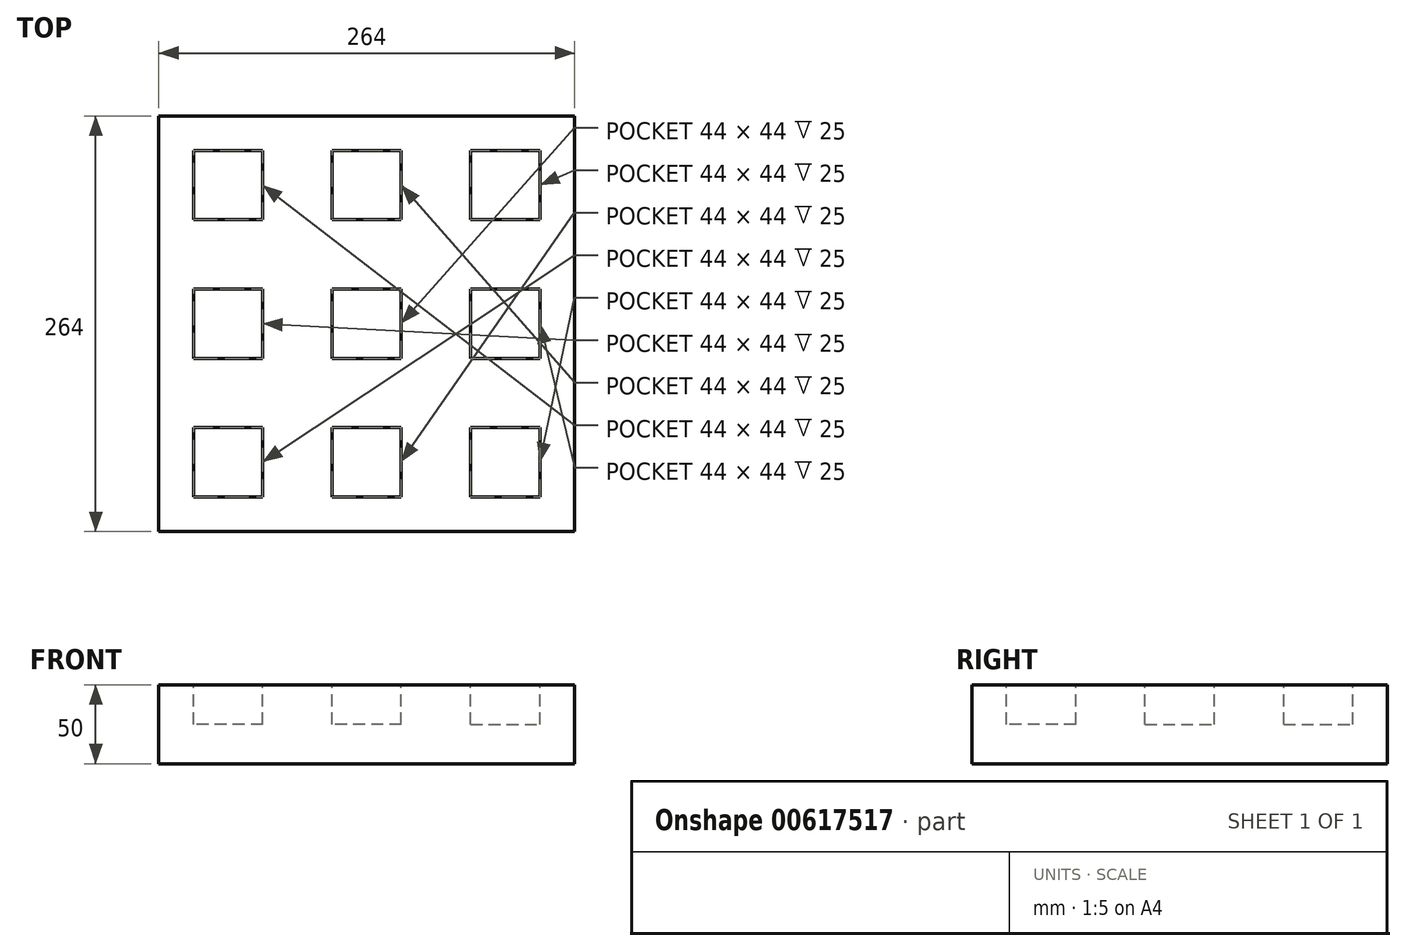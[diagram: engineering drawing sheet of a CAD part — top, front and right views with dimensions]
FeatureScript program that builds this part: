
annotation { "Feature Type Name" : "Feature", "Feature Type Description" : "" }
export const myFeature = defineFeature(function(context is Context, id is Id, definition is map)
    precondition{}
    {
        {
            var Q0;
            Q0=qCreatedBy(makeId("Top.planeOp"),FACE);
            var sketch = newSketch(context, id + "F0", { "sketchPlane" : qUnion([Q0])});
            skLineSegment(sketch, "E0.bottom", {"start": v(22, -22) * mm, "end": v(-22, -22) * mm});
            skLineSegment(sketch, "E0.top", {"start": v(22, 22) * mm, "end": v(-22, 22) * mm});
            skLineSegment(sketch, "E0.left", {"start": v(22, -22) * mm, "end": v(22, 22) * mm});
            skLineSegment(sketch, "E0.right", {"start": v(-22, -22) * mm, "end": v(-22, 22) * mm});
            skPoint(sketch, "E0.middle", {"position": v(0, 0) * mm});
            skLineSegment(sketch, "E1.bottom", {"start": v(-66, -22) * mm, "end": v(-110, -22) * mm});
            skLineSegment(sketch, "E1.top", {"start": v(-66, 22) * mm, "end": v(-110, 22) * mm});
            skLineSegment(sketch, "E1.left", {"start": v(-66, -22) * mm, "end": v(-66, 22) * mm});
            skLineSegment(sketch, "E1.right", {"start": v(-110, -22) * mm, "end": v(-110, 22) * mm});
            skPoint(sketch, "E1.middle", {"position": v(-88, 0) * mm});
            skPoint(sketch, "E1.middle.positionSnap0", {"position": v(-22, 0) * mm});
            skPoint(sketch, "E1.centerSnap0", {"position": v(-22, 0) * mm});
            skLineSegment(sketch, "E2.bottom", {"start": v(22, 66) * mm, "end": v(-22, 66) * mm});
            skLineSegment(sketch, "E2.top", {"start": v(22, 110) * mm, "end": v(-22, 110) * mm});
            skLineSegment(sketch, "E2.left", {"start": v(22, 66) * mm, "end": v(22, 110) * mm});
            skLineSegment(sketch, "E2.right", {"start": v(-22, 66) * mm, "end": v(-22, 110) * mm});
            skLineSegment(sketch, "E3.bottom", {"start": v(-66, 66) * mm, "end": v(-110, 66) * mm});
            skLineSegment(sketch, "E3.top", {"start": v(-66, 110) * mm, "end": v(-110, 110) * mm});
            skLineSegment(sketch, "E3.left", {"start": v(-66, 66) * mm, "end": v(-66, 110) * mm});
            skLineSegment(sketch, "E3.right", {"start": v(-110, 66) * mm, "end": v(-110, 110) * mm});
            skLineSegment(sketch, "E4.bottom", {"start": v(-132, 132) * mm, "end": v(132, 132) * mm});
            skLineSegment(sketch, "E4.top", {"start": v(-132, -132) * mm, "end": v(132, -132) * mm});
            skLineSegment(sketch, "E4.left", {"start": v(-132, 132) * mm, "end": v(-132, -132) * mm});
            skLineSegment(sketch, "E4.right", {"start": v(132, 132) * mm, "end": v(132, -132) * mm});
            skSolve(sketch);
        }
        {
            var Q0;
            Q0=makeQuery(id+"F0.imprint","IMPRINT",FACE,{"disambiguationData":[TD([[makeQuery(id+"F0.imprint","IMPRINT",EDGE,{"derivedFrom":sQuery(id+"F0.wireOp",EDGE,"E1.bottom")}),-1.0]])]});
            var Q1;
            Q1=makeQuery(id+"F0.imprint","IMPRINT",FACE,{"disambiguationData":[TD([[makeQuery(id+"F0.imprint","IMPRINT",EDGE,{"derivedFrom":sQuery(id+"F0.wireOp",EDGE,"E3.bottom")}),-1.0]])]});
            var Q2;
            Q2=makeQuery(id+"F0.imprint","IMPRINT",FACE,{"disambiguationData":[TD([[makeQuery(id+"F0.imprint","IMPRINT",EDGE,{"derivedFrom":sQuery(id+"F0.wireOp",EDGE,"E2.bottom")}),-1.0]])]});
            var Q3;
            Q3=makeQuery(id+"F0.imprint","IMPRINT",FACE,{"disambiguationData":[TD([[makeQuery(id+"F0.imprint","IMPRINT",EDGE,{"derivedFrom":sQuery(id+"F0.wireOp",EDGE,"E0.bottom")}),-1.0]])]});
            extrude(context, id + "F1", {"entities" : qUnion([Q0, Q1, Q2, Q3]), "oppositeDirection" : true, "depth" : 25 * mm, "offsetDistance" : 25 * mm});
        }
        {
            var Q0;
            Q0=makeQuery(id+"F1.opExtrude","SWEPT_BODY",BODY,{"disambiguationData":[OSD([sQuery(id+"F0.wireOp",EDGE,"E1.bottom"),sQuery(id+"F0.wireOp",EDGE,"E1.top"),sQuery(id+"F0.wireOp",EDGE,"E1.left"),sQuery(id+"F0.wireOp",EDGE,"E1.right")])]});
            var Q1;
            Q1=makeQuery(id+"F1.opExtrude","SWEPT_BODY",BODY,{"disambiguationData":[OSD([sQuery(id+"F0.wireOp",EDGE,"E3.bottom"),sQuery(id+"F0.wireOp",EDGE,"E3.top"),sQuery(id+"F0.wireOp",EDGE,"E3.left"),sQuery(id+"F0.wireOp",EDGE,"E3.right")])]});
            var Q2;
            Q2=qCreatedBy(makeId("Right.planeOp"),FACE);
            mirror(context, id + "F2", {"entities" : qUnion([Q0, Q1]), "mirrorPlane" : qUnion([Q2])});
        }
        {
            var Q0;
            Q0=makeQuery(id+"F1.opExtrude","SWEPT_BODY",BODY,{"disambiguationData":[OSD([sQuery(id+"F0.wireOp",EDGE,"E3.bottom"),sQuery(id+"F0.wireOp",EDGE,"E3.top"),sQuery(id+"F0.wireOp",EDGE,"E3.left"),sQuery(id+"F0.wireOp",EDGE,"E3.right")])]});
            var Q1;
            Q1=makeQuery(id+"F1.opExtrude","SWEPT_BODY",BODY,{"disambiguationData":[OSD([sQuery(id+"F0.wireOp",EDGE,"E2.bottom"),sQuery(id+"F0.wireOp",EDGE,"E2.top"),sQuery(id+"F0.wireOp",EDGE,"E2.left"),sQuery(id+"F0.wireOp",EDGE,"E2.right")])]});
            var Q2;
            Q2=makeQuery(id+"F2.opPattern","COPY",BODY,{"derivedFrom":makeQuery(id+"F1.opExtrude","SWEPT_BODY",BODY,{"disambiguationData":[OSD([sQuery(id+"F0.wireOp",EDGE,"E3.bottom"),sQuery(id+"F0.wireOp",EDGE,"E3.top"),sQuery(id+"F0.wireOp",EDGE,"E3.left"),sQuery(id+"F0.wireOp",EDGE,"E3.right")])]}),"instanceName":"1"});
            var Q3;
            Q3=qCreatedBy(makeId("Front.planeOp"),FACE);
            mirror(context, id + "F3", {"entities" : qUnion([Q0, Q1, Q2]), "mirrorPlane" : qUnion([Q3])});
        }
        {
            var Q0;
            Q0=makeQuery(id+"F0.imprint","IMPRINT",FACE,{"disambiguationData":[TD([[makeQuery(id+"F0.imprint","IMPRINT",EDGE,{"derivedFrom":sQuery(id+"F0.wireOp",EDGE,"E0.bottom")}),1.0]])]});
            var Q1;
            Q1=makeQuery(id+"F0.imprint","IMPRINT",FACE,{"disambiguationData":[TD([[makeQuery(id+"F0.imprint","IMPRINT",EDGE,{"derivedFrom":sQuery(id+"F0.wireOp",EDGE,"E1.bottom")}),-1.0]])]});
            var Q2;
            Q2=makeQuery(id+"F0.imprint","IMPRINT",FACE,{"disambiguationData":[TD([[makeQuery(id+"F0.imprint","IMPRINT",EDGE,{"derivedFrom":sQuery(id+"F0.wireOp",EDGE,"E0.bottom")}),-1.0]])]});
            var Q3;
            Q3=makeQuery(id+"F0.imprint","IMPRINT",FACE,{"disambiguationData":[TD([[makeQuery(id+"F0.imprint","IMPRINT",EDGE,{"derivedFrom":sQuery(id+"F0.wireOp",EDGE,"E3.bottom")}),-1.0]])]});
            var Q4;
            Q4=makeQuery(id+"F0.imprint","IMPRINT",FACE,{"disambiguationData":[TD([[makeQuery(id+"F0.imprint","IMPRINT",EDGE,{"derivedFrom":sQuery(id+"F0.wireOp",EDGE,"E2.bottom")}),-1.0]])]});
            extrude(context, id + "F4", {"entities" : qUnion([Q0, Q1, Q2, Q3, Q4]), "oppositeDirection" : true, "depth" : 50 * mm, "offsetDistance" : 25 * mm});
        }
        {
            var Q0;
            Q0=makeQuery(id+"F1.opExtrude","SWEPT_BODY",BODY,{"disambiguationData":[OSD([sQuery(id+"F0.wireOp",EDGE,"E0.bottom"),sQuery(id+"F0.wireOp",EDGE,"E0.top"),sQuery(id+"F0.wireOp",EDGE,"E0.left"),sQuery(id+"F0.wireOp",EDGE,"E0.right")])]});
            var Q1;
            Q1=makeQuery(id+"F1.opExtrude","SWEPT_BODY",BODY,{"disambiguationData":[OSD([sQuery(id+"F0.wireOp",EDGE,"E1.bottom"),sQuery(id+"F0.wireOp",EDGE,"E1.top"),sQuery(id+"F0.wireOp",EDGE,"E1.left"),sQuery(id+"F0.wireOp",EDGE,"E1.right")])]});
            var Q2;
            Q2=makeQuery(id+"F1.opExtrude","SWEPT_BODY",BODY,{"disambiguationData":[OSD([sQuery(id+"F0.wireOp",EDGE,"E2.bottom"),sQuery(id+"F0.wireOp",EDGE,"E2.top"),sQuery(id+"F0.wireOp",EDGE,"E2.left"),sQuery(id+"F0.wireOp",EDGE,"E2.right")])]});
            var Q3;
            Q3=makeQuery(id+"F1.opExtrude","SWEPT_BODY",BODY,{"disambiguationData":[OSD([sQuery(id+"F0.wireOp",EDGE,"E3.bottom"),sQuery(id+"F0.wireOp",EDGE,"E3.top"),sQuery(id+"F0.wireOp",EDGE,"E3.left"),sQuery(id+"F0.wireOp",EDGE,"E3.right")])]});
            var Q4;
            Q4=makeQuery(id+"F2.opPattern","COPY",BODY,{"derivedFrom":makeQuery(id+"F1.opExtrude","SWEPT_BODY",BODY,{"disambiguationData":[OSD([sQuery(id+"F0.wireOp",EDGE,"E1.bottom"),sQuery(id+"F0.wireOp",EDGE,"E1.top"),sQuery(id+"F0.wireOp",EDGE,"E1.left"),sQuery(id+"F0.wireOp",EDGE,"E1.right")])]}),"instanceName":"1"});
            var Q5;
            Q5=makeQuery(id+"F2.opPattern","COPY",BODY,{"derivedFrom":makeQuery(id+"F1.opExtrude","SWEPT_BODY",BODY,{"disambiguationData":[OSD([sQuery(id+"F0.wireOp",EDGE,"E3.bottom"),sQuery(id+"F0.wireOp",EDGE,"E3.top"),sQuery(id+"F0.wireOp",EDGE,"E3.left"),sQuery(id+"F0.wireOp",EDGE,"E3.right")])]}),"instanceName":"1"});
            var Q6;
            Q6=makeQuery(id+"F3.opPattern","COPY",BODY,{"derivedFrom":makeQuery(id+"F1.opExtrude","SWEPT_BODY",BODY,{"disambiguationData":[OSD([sQuery(id+"F0.wireOp",EDGE,"E2.bottom"),sQuery(id+"F0.wireOp",EDGE,"E2.top"),sQuery(id+"F0.wireOp",EDGE,"E2.left"),sQuery(id+"F0.wireOp",EDGE,"E2.right")])]}),"instanceName":"1"});
            var Q7;
            Q7=makeQuery(id+"F3.opPattern","COPY",BODY,{"derivedFrom":makeQuery(id+"F1.opExtrude","SWEPT_BODY",BODY,{"disambiguationData":[OSD([sQuery(id+"F0.wireOp",EDGE,"E3.bottom"),sQuery(id+"F0.wireOp",EDGE,"E3.top"),sQuery(id+"F0.wireOp",EDGE,"E3.left"),sQuery(id+"F0.wireOp",EDGE,"E3.right")])]}),"instanceName":"1"});
            var Q8;
            Q8=makeQuery(id+"F3.opPattern","COPY",BODY,{"derivedFrom":makeQuery(id+"F2.opPattern","COPY",BODY,{"derivedFrom":makeQuery(id+"F1.opExtrude","SWEPT_BODY",BODY,{"disambiguationData":[OSD([sQuery(id+"F0.wireOp",EDGE,"E3.bottom"),sQuery(id+"F0.wireOp",EDGE,"E3.top"),sQuery(id+"F0.wireOp",EDGE,"E3.left"),sQuery(id+"F0.wireOp",EDGE,"E3.right")])]}),"instanceName":"1"}),"instanceName":"1"});
            var Q9;
            Q9=makeQuery(id+"F4.opExtrude","SWEPT_BODY",BODY,{"disambiguationData":[OSD([sQuery(id+"F0.wireOp",EDGE,"E4.bottom"),sQuery(id+"F0.wireOp",EDGE,"E4.top"),sQuery(id+"F0.wireOp",EDGE,"E4.left"),sQuery(id+"F0.wireOp",EDGE,"E4.right")])]});
            booleanBodies(context, id + "F5", {"operationType" : BooleanOperationType.SUBTRACTION, "tools" : qUnion([Q0, Q1, Q2, Q3, Q4, Q5, Q6, Q7, Q8]), "targets" : qUnion([Q9])});
        }
    });
